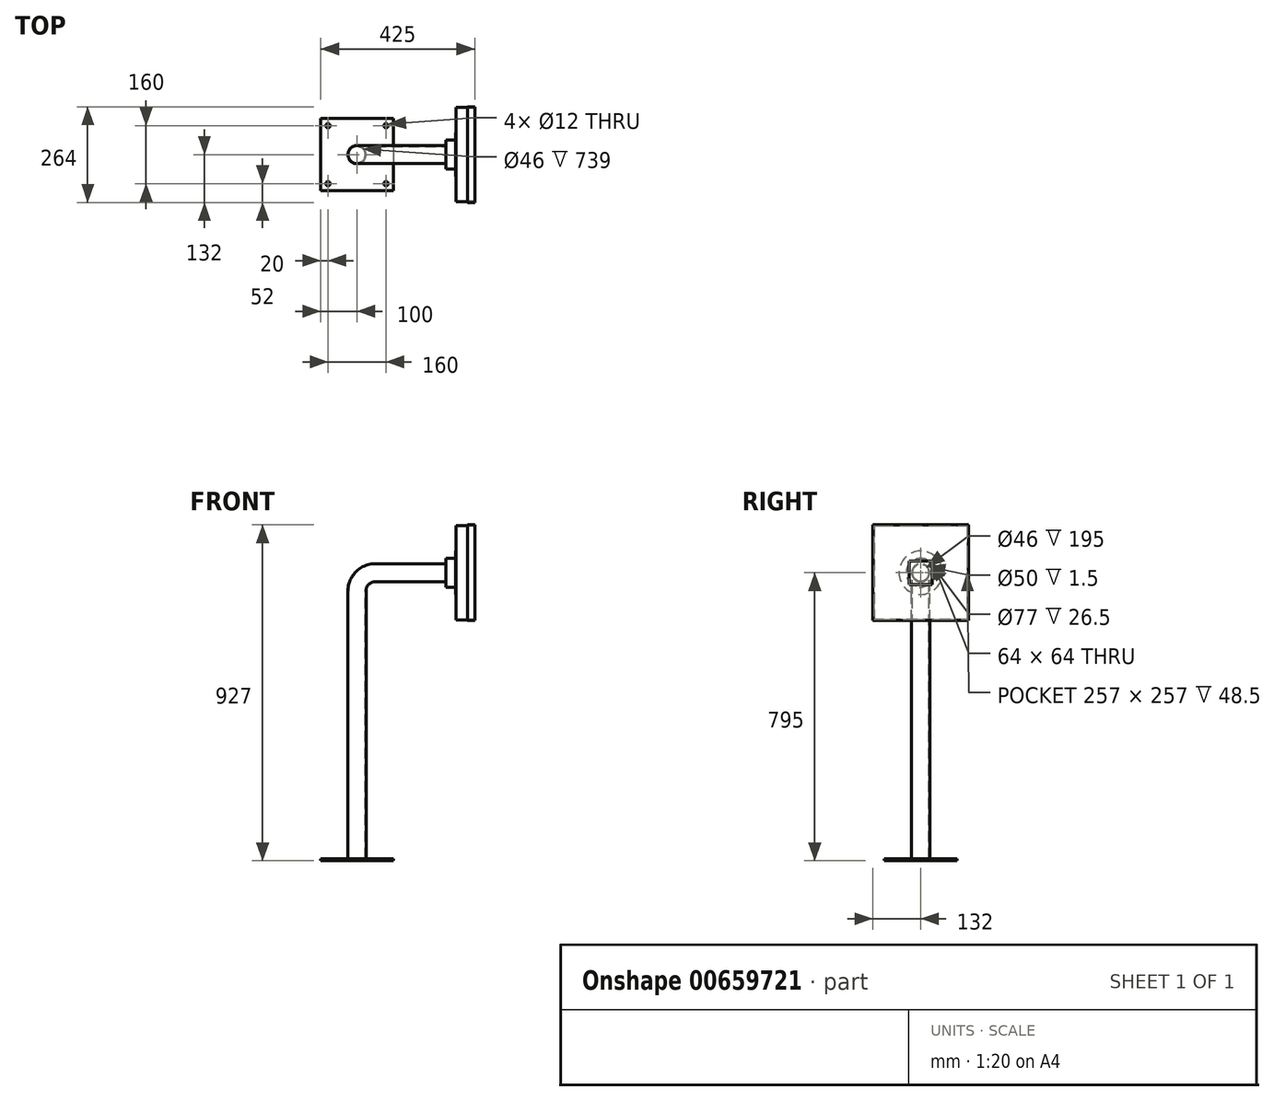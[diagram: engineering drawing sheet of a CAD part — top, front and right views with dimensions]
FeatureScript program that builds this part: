
annotation { "Feature Type Name" : "Feature", "Feature Type Description" : "" }
export const myFeature = defineFeature(function(context is Context, id is Id, definition is map)
    precondition{}
    {
        {
            var Q0;
            Q0=qCreatedBy(makeId("Top.planeOp"),FACE);
            var sketch = newSketch(context, id + "F0", { "sketchPlane" : qUnion([Q0])});
            skLineSegment(sketch, "E0.bottom", {"start": v(100, 100) * mm, "end": v(-100, 100) * mm});
            skLineSegment(sketch, "E0.top", {"start": v(100, -100) * mm, "end": v(-100, -100) * mm});
            skLineSegment(sketch, "E0.left", {"start": v(100, 100) * mm, "end": v(100, -100) * mm});
            skLineSegment(sketch, "E0.right", {"start": v(-100, 100) * mm, "end": v(-100, -100) * mm});
            skPoint(sketch, "E0.middle", {"position": v(0, 0) * mm});
            skLineSegment(sketch, "E1.0", {"start": v(80, 80) * mm, "end": v(-80, 80) * mm, "construction": true});
            skLineSegment(sketch, "E1.1", {"start": v(80, 80) * mm, "end": v(80, -80) * mm, "construction": true});
            skLineSegment(sketch, "E1.2", {"start": v(80, -80) * mm, "end": v(-80, -80) * mm, "construction": true});
            skLineSegment(sketch, "E1.3", {"start": v(-80, 80) * mm, "end": v(-80, -80) * mm, "construction": true});
            skCircle(sketch, "E2", {"center": v(-80, 80) * mm, "radius": 6 * mm});
            skCircle(sketch, "E3", {"center": v(80, 80) * mm, "radius": 6 * mm});
            skCircle(sketch, "E4", {"center": v(80, -80) * mm, "radius": 6 * mm});
            skCircle(sketch, "E5", {"center": v(-80, -80) * mm, "radius": 6 * mm});
            skSolve(sketch);
        }
        {
            var Q0;
            Q0 = qSketchRegion(id + "F0", true);
            extrude(context, id + "F1", {"entities" : qUnion([Q0]), "depth" : 6 * mm, "offsetDistance" : 25 * mm});
        }
        {
            var Q0;
            Q0=qCreatedBy(makeId("Front.planeOp"),FACE);
            var sketch = newSketch(context, id + "F2", { "sketchPlane" : qUnion([Q0])});
            skLineSegment(sketch, "E6", {"start": v(0, 6) * mm, "end": v(0, 745) * mm});
            skLineSegment(sketch, "E7", {"start": v(50, 795) * mm, "end": v(245, 795) * mm});
            skPoint(sketch, "E8.visualSharp", {"position": v(0, 795) * mm});
            skArc(sketch, "E8.filletArc", {"start": v(50, 795) * mm, "mid": v(14.64, 780.36) * mm, "end": v(0, 745) * mm});
            skSolve(sketch);
        }
        {
            var Q0;
            Q0=makeQuery(id+"F1.opExtrude","CAP_FACE",FACE,{"disambiguationData":[OSD([sQuery(id+"F0.wireOp",EDGE,"E0.bottom"),sQuery(id+"F0.wireOp",EDGE,"E0.top"),sQuery(id+"F0.wireOp",EDGE,"E0.left"),sQuery(id+"F0.wireOp",EDGE,"E0.right"),sQuery(id+"F0.wireOp",EDGE,"E2"),sQuery(id+"F0.wireOp",EDGE,"E3"),sQuery(id+"F0.wireOp",EDGE,"E4"),sQuery(id+"F0.wireOp",EDGE,"E5")])],"isStart":false});
            var sketch = newSketch(context, id + "F3", { "sketchPlane" : qUnion([Q0])});
            skCircle(sketch, "E9", {"center": v(0, 0) * mm, "radius": 25 * mm});
            skCircle(sketch, "E10.0", {"center": v(0, 0) * mm, "radius": 23 * mm});
            skSolve(sketch);
        }
        {
            var Q0;
            Q0=makeQuery(id+"F3.imprint","IMPRINT",FACE,{"disambiguationData":[TD([[makeQuery(id+"F3.imprint","IMPRINT",EDGE,{"derivedFrom":sQuery(id+"F3.wireOp",EDGE,"E9")}),1.0]])]});
            var Q1;
            Q1=sQuery(id+"F2.wireOp",EDGE,"E6");
            var Q2;
            Q2=sQuery(id+"F2.wireOp",EDGE,"E8.filletArc");
            var Q3;
            Q3=sQuery(id+"F2.wireOp",EDGE,"E7");
            sweep(context, id + "F4", {"operationType" : NewBodyOperationType.ADD, "profiles" : qUnion([Q0]), "path" : qUnion([Q1, Q2, Q3])});
        }
        {
            var Q0;
            Q0=qCreatedBy(makeId("Front.planeOp"),FACE);
            var sketch = newSketch(context, id + "F5", { "sketchPlane" : qUnion([Q0])});
            skLineSegment(sketch, "E11", {"start": v(245, 795) * mm, "end": v(296.4, 795) * mm, "construction": true});
            skLineSegment(sketch, "E12", {"start": v(245, 820) * mm, "end": v(245, 835) * mm});
            skLineSegment(sketch, "E13", {"start": v(245, 835) * mm, "end": v(271.5, 835) * mm});
            skLineSegment(sketch, "E14", {"start": v(271.5, 835) * mm, "end": v(271.5, 855) * mm});
            skLineSegment(sketch, "E15", {"start": v(271.5, 855) * mm, "end": v(273, 855) * mm});
            skLineSegment(sketch, "E16", {"start": v(273, 855) * mm, "end": v(273, 833.5) * mm});
            skLineSegment(sketch, "E17.0", {"start": v(246.5, 833.5) * mm, "end": v(273, 833.5) * mm});
            skLineSegment(sketch, "E17.1", {"start": v(246.5, 820) * mm, "end": v(246.5, 833.5) * mm});
            skLineSegment(sketch, "E18", {"start": v(245, 820) * mm, "end": v(246.5, 820) * mm});
            skSolve(sketch);
        }
        {
            var Q0;
            Q0=makeQuery(id+"F5.imprint","IMPRINT",FACE,{"disambiguationData":[TD([[makeQuery(id+"F5.imprint","IMPRINT",EDGE,{"derivedFrom":sQuery(id+"F5.wireOp",EDGE,"E12")}),-1.0]])]});
            var Q1;
            Q1=sQuery(id+"F5.wireOp",EDGE,"E11");
            revolve(context, id + "F6", {"entities" : qUnion([Q0]), "axis" : qUnion([Q1]), "revolveType" : RevolveType.FULL});
        }
        {
            var Q0;
            Q0=makeQuery(id+"F6.opRevolve","SWEPT_FACE",FACE,{"disambiguationData":[OSD([sQuery(id+"F5.wireOp",EDGE,"E16")])]});
            var sketch = newSketch(context, id + "F7", { "sketchPlane" : qUnion([Q0])});
            skLineSegment(sketch, "E19.bottom", {"start": v(130, 925) * mm, "end": v(-130, 925) * mm});
            skLineSegment(sketch, "E19.top", {"start": v(130, 665) * mm, "end": v(-130, 665) * mm});
            skLineSegment(sketch, "E19.left", {"start": v(130, 925) * mm, "end": v(130, 665) * mm});
            skLineSegment(sketch, "E19.right", {"start": v(-130, 925) * mm, "end": v(-130, 665) * mm});
            skPoint(sketch, "E19.middle", {"position": v(0, 795) * mm});
            skSolve(sketch);
        }
        {
            var Q0;
            Q0 = qSketchRegion(id + "F7", true);
            extrude(context, id + "F8", {"entities" : qUnion([Q0]), "depth" : 50 * mm, "offsetDistance" : 25 * mm});
        }
        {
            var Q0;
            Q0=makeQuery(id+"F8.opExtrude","CAP_FACE",FACE,{"disambiguationData":[OSD([sQuery(id+"F7.wireOp",EDGE,"E19.bottom"),sQuery(id+"F7.wireOp",EDGE,"E19.top"),sQuery(id+"F7.wireOp",EDGE,"E19.left"),sQuery(id+"F7.wireOp",EDGE,"E19.right")])],"isStart":false});
            shell(context, id + "F9", {"entities" : qUnion([Q0]), "thickness" : 1.5 * mm});
        }
        {
            var Q0;
            Q0=makeQuery(id+"F8.opExtrude","CAP_FACE",FACE,{"disambiguationData":[OSD([sQuery(id+"F7.wireOp",EDGE,"E19.bottom"),sQuery(id+"F7.wireOp",EDGE,"E19.top"),sQuery(id+"F7.wireOp",EDGE,"E19.left"),sQuery(id+"F7.wireOp",EDGE,"E19.right")])],"isStart":true});
            cPlane(context, id + "F10", {"entities" : qUnion([Q0]), "cplaneType" : CPlaneType.OFFSET, "offset" : 32 * mm, "oppositeDirection" : true, "width" : 150 * mm, "height" : 150 * mm});
        }
        {
            var Q0;
            Q0=qCreatedBy(id+"F10.planeOp",FACE);
            var sketch = newSketch(context, id + "F11", { "sketchPlane" : qUnion([Q0])});
            skLineSegment(sketch, "E20.0", {"start": v(132, 927) * mm, "end": v(132, 663) * mm});
            skLineSegment(sketch, "E20.1", {"start": v(-132, 927) * mm, "end": v(132, 927) * mm});
            skLineSegment(sketch, "E20.2", {"start": v(-132, 927) * mm, "end": v(-132, 663) * mm});
            skLineSegment(sketch, "E20.3", {"start": v(-132, 663) * mm, "end": v(132, 663) * mm});
            skSolve(sketch);
        }
        {
            var Q0;
            Q0 = qSketchRegion(id + "F11", true);
            extrude(context, id + "F12", {"entities" : qUnion([Q0]), "oppositeDirection" : true, "depth" : 20 * mm, "offsetDistance" : 25 * mm});
        }
        {
            var Q0;
            Q0=makeQuery(id+"F12.opExtrude","CAP_FACE",FACE,{"disambiguationData":[OSD([sQuery(id+"F11.wireOp",EDGE,"E20.0"),sQuery(id+"F11.wireOp",EDGE,"E20.1"),sQuery(id+"F11.wireOp",EDGE,"E20.2"),sQuery(id+"F11.wireOp",EDGE,"E20.3")])],"isStart":true});
            shell(context, id + "F13", {"entities" : qUnion([Q0]), "thickness" : 1.5 * mm});
        }
        {
            var Q0;
            Q0=makeQuery(id+"F12.opExtrude","CAP_FACE",FACE,{"disambiguationData":[OSD([sQuery(id+"F11.wireOp",EDGE,"E20.0"),sQuery(id+"F11.wireOp",EDGE,"E20.1"),sQuery(id+"F11.wireOp",EDGE,"E20.2"),sQuery(id+"F11.wireOp",EDGE,"E20.3")])],"isStart":false});
            var sketch = newSketch(context, id + "F14", { "sketchPlane" : qUnion([Q0])});
            skLineSegment(sketch, "E21.0", {"start": v(32, 827) * mm, "end": v(-32, 827) * mm});
            skLineSegment(sketch, "E21.1", {"start": v(32, 827) * mm, "end": v(32, 763) * mm});
            skLineSegment(sketch, "E21.2", {"start": v(32, 763) * mm, "end": v(-32, 763) * mm});
            skLineSegment(sketch, "E21.3", {"start": v(-32, 827) * mm, "end": v(-32, 763) * mm});
            skSolve(sketch);
        }
        {
            var Q0;
            Q0 = qSketchRegion(id + "F14", true);
            extrude(context, id + "F15", {"entities" : qUnion([Q0]), "operationType" : NewBodyOperationType.REMOVE, "endBound" : BoundingType.UP_TO_NEXT, "oppositeDirection" : true, "depth" : 25 * mm, "offsetDistance" : 25 * mm});
        }
    });
